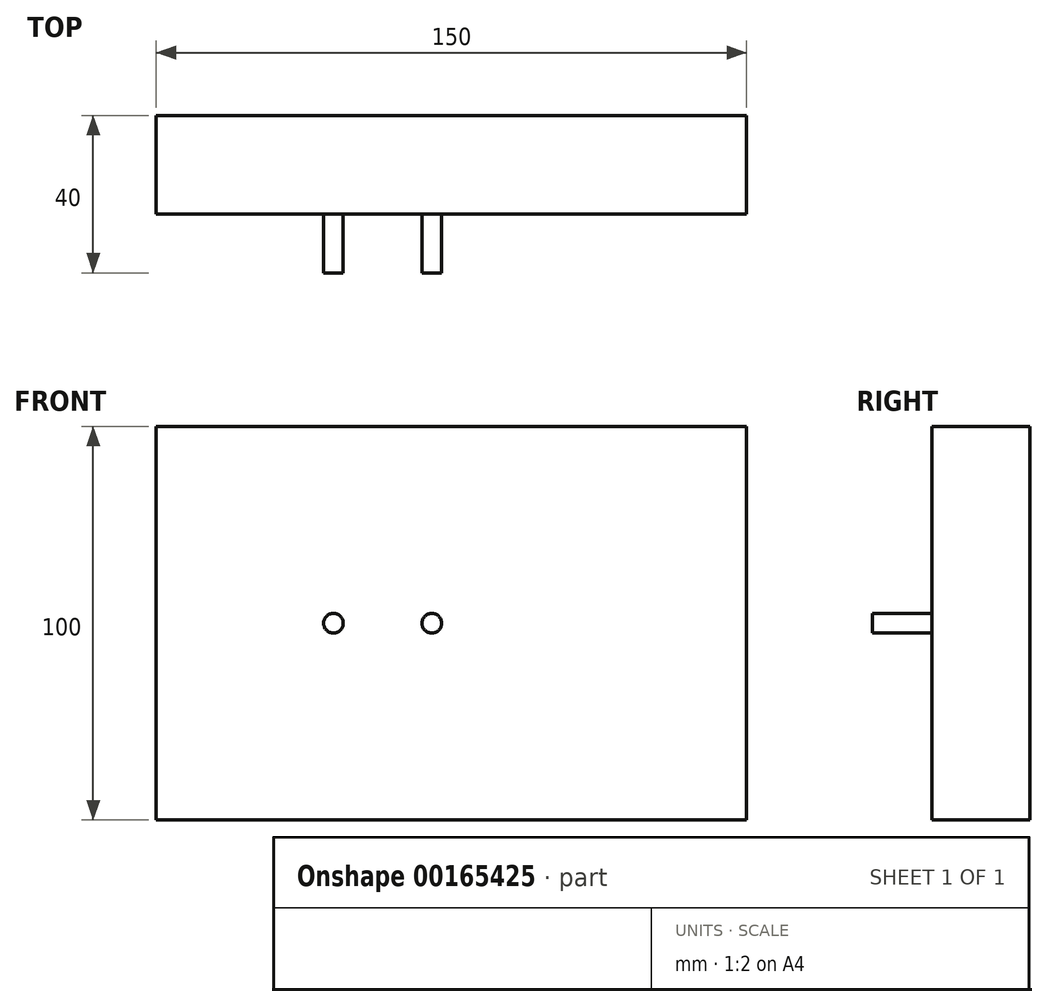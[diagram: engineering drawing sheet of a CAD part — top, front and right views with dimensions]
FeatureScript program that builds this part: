
annotation { "Feature Type Name" : "Feature", "Feature Type Description" : "" }
export const myFeature = defineFeature(function(context is Context, id is Id, definition is map)
    precondition{}
    {
        {
            var Q0;
            Q0=qCreatedBy(makeId("Front.planeOp"),FACE);
            var sketch = newSketch(context, id + "F0", { "sketchPlane" : qUnion([Q0])});
            skLineSegment(sketch, "E0.bottom", {"start": v(-75, 50) * mm, "end": v(75, 50) * mm});
            skLineSegment(sketch, "E0.top", {"start": v(-75, -50) * mm, "end": v(75, -50) * mm});
            skLineSegment(sketch, "E0.left", {"start": v(-75, 50) * mm, "end": v(-75, -50) * mm});
            skLineSegment(sketch, "E0.right", {"start": v(75, 50) * mm, "end": v(75, -50) * mm});
            skLineSegment(sketch, "E1", {"start": v(0, 0) * mm, "end": v(0, 28.17) * mm});
            skSolve(sketch);
        }
        {
            var Q0;
            Q0=makeQuery(id+"F0.imprint","IMPRINT",FACE,{"disambiguationData":[TD([[makeQuery(id+"F0.imprint","IMPRINT",EDGE,{"derivedFrom":sQuery(id+"F0.wireOp",EDGE,"E0.bottom")}),-1.0]])]});
            extrude(context, id + "F1", {"entities" : qUnion([Q0]), "depth" : 25 * mm});
        }
        {
            var Q0;
            Q0=makeQuery(id+"F1.opExtrude","CAP_FACE",FACE,{"disambiguationData":[OSD([sQuery(id+"F0.wireOp",EDGE,"E0.bottom"),sQuery(id+"F0.wireOp",EDGE,"E0.top"),sQuery(id+"F0.wireOp",EDGE,"E0.left"),sQuery(id+"F0.wireOp",EDGE,"E0.right")])],"isStart":false});
            var sketch = newSketch(context, id + "F2", { "sketchPlane" : qUnion([Q0])});
            skLineSegment(sketch, "E2", {"start": v(0, 0) * mm, "end": v(-30, 0) * mm});
            skCircle(sketch, "E3", {"center": v(-30, 0) * mm, "radius": 2.5 * mm});
            skSolve(sketch);
        }
        {
            var Q0;
            Q0=makeQuery(id+"F2.imprint","IMPRINT",FACE,{"disambiguationData":[TD([[makeQuery(id+"F2.imprint","IMPRINT",EDGE,{"derivedFrom":sQuery(id+"F2.wireOp",EDGE,"E3")}),1.0]])]});
            extrude(context, id + "F3", {"entities" : qUnion([Q0]), "operationType" : NewBodyOperationType.ADD, "depth" : 15 * mm});
        }
        {
            var Q0;
            Q0=makeQuery(id+"F1.opExtrude","CAP_FACE",FACE,{"disambiguationData":[OSD([sQuery(id+"F0.wireOp",EDGE,"E0.bottom"),sQuery(id+"F0.wireOp",EDGE,"E0.top"),sQuery(id+"F0.wireOp",EDGE,"E0.left"),sQuery(id+"F0.wireOp",EDGE,"E0.right")])],"isStart":false});
            var sketch = newSketch(context, id + "F4", { "sketchPlane" : qUnion([Q0])});
            skLineSegment(sketch, "E4", {"start": v(0, 0) * mm, "end": v(-5, 0) * mm});
            skCircle(sketch, "E5", {"center": v(-5, 0) * mm, "radius": 2.5 * mm});
            skSolve(sketch);
        }
        {
            var Q0;
            Q0=makeQuery(id+"F4.imprint","IMPRINT",FACE,{"disambiguationData":[TD([[makeQuery(id+"F4.imprint","IMPRINT",EDGE,{"derivedFrom":sQuery(id+"F4.wireOp",EDGE,"E5")}),1.0]])]});
            extrude(context, id + "F5", {"entities" : qUnion([Q0]), "operationType" : NewBodyOperationType.ADD, "depth" : 15 * mm});
        }
    });
